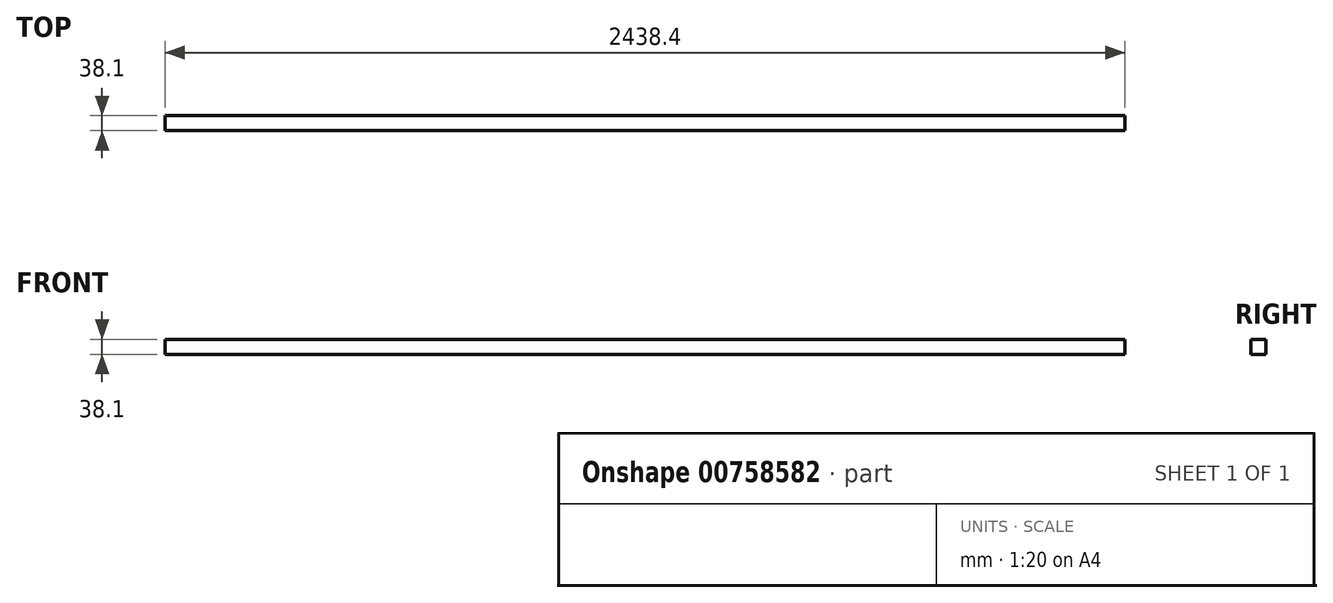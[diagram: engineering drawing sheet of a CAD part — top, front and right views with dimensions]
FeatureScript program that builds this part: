
annotation { "Feature Type Name" : "Feature", "Feature Type Description" : "" }
export const myFeature = defineFeature(function(context is Context, id is Id, definition is map)
    precondition{}
    {
        {
            var Q0;
            Q0=qCreatedBy(makeId("Front.planeOp"),FACE);
            var sketch = newSketch(context, id + "F0", { "sketchPlane" : qUnion([Q0])});
            skLineSegment(sketch, "E0.bottom", {"start": v(-1219.2, 19.05) * mm, "end": v(1219.2, 19.05) * mm});
            skLineSegment(sketch, "E0.top", {"start": v(-1219.2, -19.05) * mm, "end": v(1219.2, -19.05) * mm});
            skLineSegment(sketch, "E0.left", {"start": v(-1219.2, 19.05) * mm, "end": v(-1219.2, -19.05) * mm});
            skLineSegment(sketch, "E0.right", {"start": v(1219.2, 19.05) * mm, "end": v(1219.2, -19.05) * mm});
            skPoint(sketch, "E0.middle", {"position": v(0, 0) * mm});
            skSolve(sketch);
        }
        {
            var Q0;
            Q0=makeQuery(id+"F0.imprint","IMPRINT",FACE,{"disambiguationData":[TD([[makeQuery(id+"F0.imprint","IMPRINT",EDGE,{"derivedFrom":sQuery(id+"F0.wireOp",EDGE,"E0.bottom")}),-1.0]])]});
            extrude(context, id + "F1", {"entities" : qUnion([Q0]), "endBound" : BoundingType.SYMMETRIC, "depth" : 38.1 * mm, "offsetDistance" : 25.4 * mm});
        }
    });
